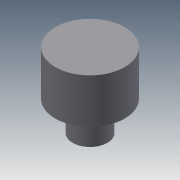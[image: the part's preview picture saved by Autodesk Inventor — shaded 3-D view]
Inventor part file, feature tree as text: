
AUTODESK INVENTOR PART (.ipt)
format: ipt  version: 2013 (Build 170138000, 138)  size: 87,040 bytes
history: native  units: mm
features: sketch x3, extrude x2, plane x1, hole x1
ambient origin geometry x8: Origin, YZ Plane, XZ Plane, XY Plane, X Axis, Y Axis, Z Axis, Center Point
bodies: Solid1 (feature_tree)
feature tree (7):
  extrude  "Extrusion1"  Depth=9.0mm TaperAngle=0.0deg
  plane  "Work Plane1"
  hole  "Hole1"  [1 undecoded]
  extrude  "Extrusion3"  Depth=6.0mm TaperAngle=0.0deg
  sketch  "Sketch1"  dims[d0=14.0mm d1=9.0mm d2=0.0mm]
  sketch  "Sketch3"  dims[d9=2.4mm]
  sketch  "Sketch4"  dims[d10=2.459mm d11=7.0mm d12=4.0mm d13=2.0mm d14=90.0deg d15=7.0mm d16=0.0mm d17=7.0mm d18=6.0mm d19=0.0mm]
note: 1 required parameter value undecoded (feature->parameter linkage not recoverable at this tier; creation-order binding heuristic only, values carry confidence <= 0.55)
